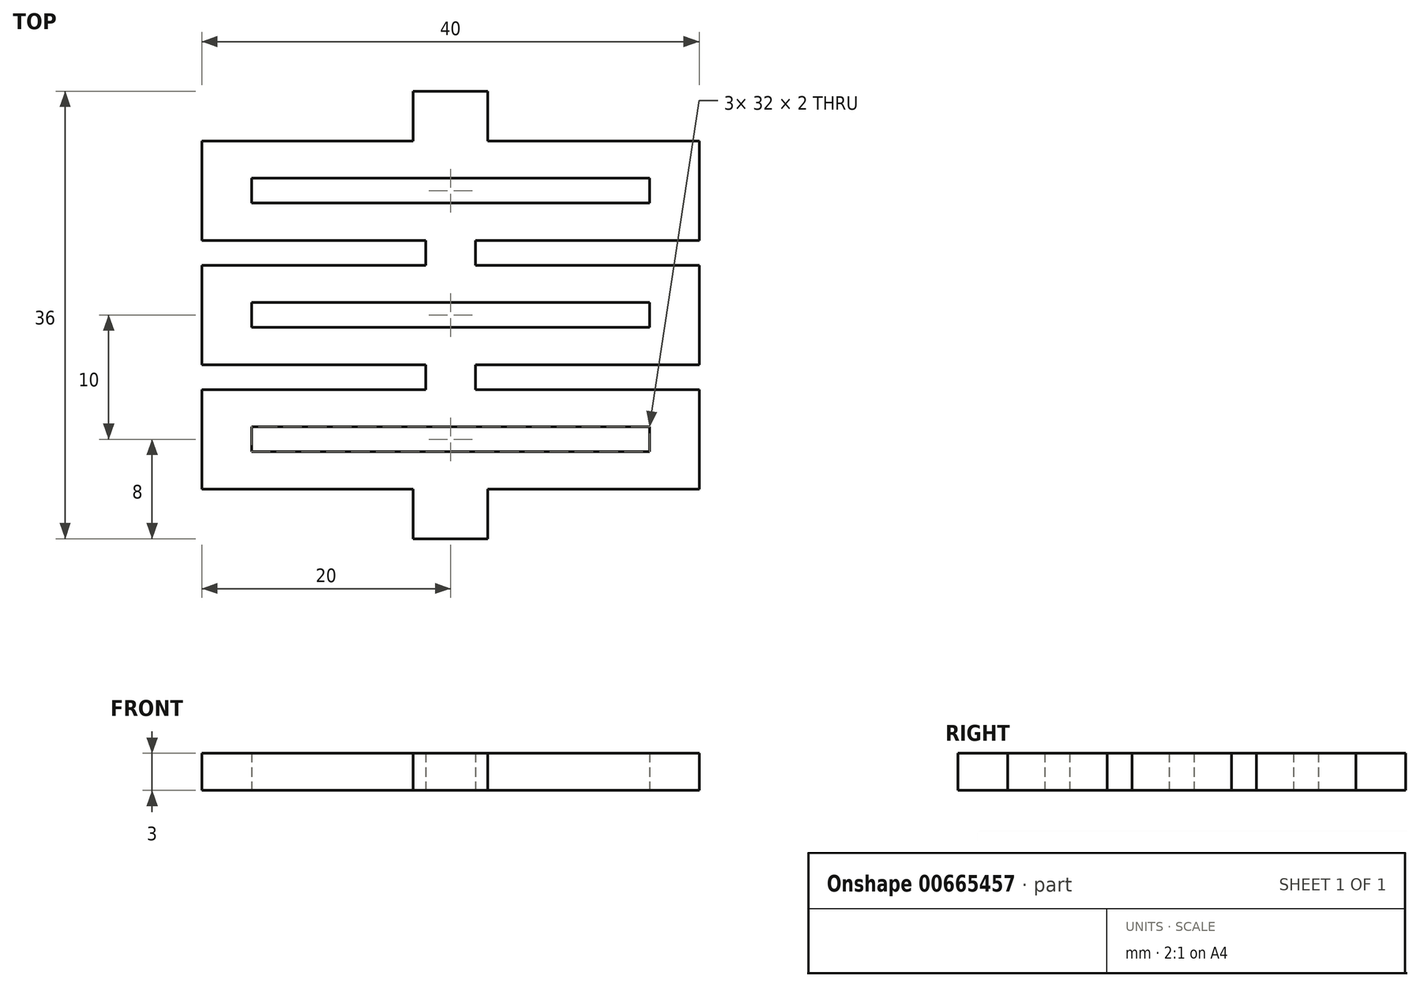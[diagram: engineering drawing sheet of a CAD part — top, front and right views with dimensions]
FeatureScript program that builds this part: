
annotation { "Feature Type Name" : "Feature", "Feature Type Description" : "" }
export const myFeature = defineFeature(function(context is Context, id is Id, definition is map)
    precondition{}
    {
        {
            var Q0;
            Q0=qCreatedBy(makeId("Top.planeOp"),FACE);
            var sketch = newSketch(context, id + "F0", { "sketchPlane" : qUnion([Q0])});
            skLineSegment(sketch, "E0.bottom", {"start": v(-3, 0) * mm, "end": v(0, 0) * mm});
            skLineSegment(sketch, "E0.top", {"start": v(-3, -4) * mm, "end": v(0, -4) * mm});
            skLineSegment(sketch, "E0.left", {"start": v(-3, 0) * mm, "end": v(-3, -4) * mm});
            skLineSegment(sketch, "E1.bottom", {"start": v(-20, -4) * mm, "end": v(0, -4) * mm});
            skLineSegment(sketch, "E1.top", {"start": v(-20, -7) * mm, "end": v(0, -7) * mm});
            skLineSegment(sketch, "E1.left", {"start": v(-20, -4) * mm, "end": v(-20, -7) * mm});
            skLineSegment(sketch, "E2.bottom", {"start": v(-20, -7) * mm, "end": v(-16, -7) * mm});
            skLineSegment(sketch, "E2.top", {"start": v(-20, -9) * mm, "end": v(-16, -9) * mm});
            skLineSegment(sketch, "E2.left", {"start": v(-20, -7) * mm, "end": v(-20, -9) * mm});
            skLineSegment(sketch, "E2.right", {"start": v(-16, -7) * mm, "end": v(-16, -9) * mm});
            skLineSegment(sketch, "E3.bottom", {"start": v(-16, -9) * mm, "end": v(0, -9) * mm});
            skLineSegment(sketch, "E3.top", {"start": v(-20, -12) * mm, "end": v(0, -12) * mm});
            skLineSegment(sketch, "E3.left", {"start": v(-20, -9) * mm, "end": v(-20, -12) * mm});
            skLineSegment(sketch, "E4.bottom", {"start": v(-2, -12) * mm, "end": v(0, -12) * mm});
            skLineSegment(sketch, "E4.top", {"start": v(-2, -14) * mm, "end": v(0, -14) * mm});
            skLineSegment(sketch, "E4.left", {"start": v(-2, -12) * mm, "end": v(-2, -14) * mm});
            skLineSegment(sketch, "E5.bottom", {"start": v(-20, -14) * mm, "end": v(0, -14) * mm});
            skLineSegment(sketch, "E5.top", {"start": v(-20, -17) * mm, "end": v(0, -17) * mm});
            skLineSegment(sketch, "E5.left", {"start": v(-20, -14) * mm, "end": v(-20, -17) * mm});
            skLineSegment(sketch, "E6.bottom", {"start": v(-20, -17) * mm, "end": v(-16, -17) * mm});
            skLineSegment(sketch, "E6.top", {"start": v(-20, -19) * mm, "end": v(-16, -19) * mm});
            skLineSegment(sketch, "E6.left", {"start": v(-20, -17) * mm, "end": v(-20, -19) * mm});
            skLineSegment(sketch, "E6.right", {"start": v(-16, -17) * mm, "end": v(-16, -19) * mm});
            skLineSegment(sketch, "E7.bottom", {"start": v(-20, -19) * mm, "end": v(0, -19) * mm});
            skLineSegment(sketch, "E7.top", {"start": v(-20, -22) * mm, "end": v(0, -22) * mm});
            skLineSegment(sketch, "E7.left", {"start": v(-20, -19) * mm, "end": v(-20, -22) * mm});
            skLineSegment(sketch, "E8.bottom", {"start": v(-2, -22) * mm, "end": v(0, -22) * mm});
            skLineSegment(sketch, "E8.top", {"start": v(-2, -24) * mm, "end": v(0, -24) * mm});
            skLineSegment(sketch, "E8.left", {"start": v(-2, -22) * mm, "end": v(-2, -24) * mm});
            skLineSegment(sketch, "E9.bottom", {"start": v(-20, -24) * mm, "end": v(0, -24) * mm});
            skLineSegment(sketch, "E9.top", {"start": v(-20, -27) * mm, "end": v(0, -27) * mm});
            skLineSegment(sketch, "E9.left", {"start": v(-20, -24) * mm, "end": v(-20, -27) * mm});
            skLineSegment(sketch, "E10.bottom", {"start": v(-20, -27) * mm, "end": v(-16, -27) * mm});
            skLineSegment(sketch, "E10.top", {"start": v(-20, -29) * mm, "end": v(-16, -29) * mm});
            skLineSegment(sketch, "E10.left", {"start": v(-20, -27) * mm, "end": v(-20, -29) * mm});
            skLineSegment(sketch, "E10.right", {"start": v(-16, -27) * mm, "end": v(-16, -29) * mm});
            skLineSegment(sketch, "E11.bottom", {"start": v(-20, -29) * mm, "end": v(0, -29) * mm});
            skLineSegment(sketch, "E11.top", {"start": v(-20, -32) * mm, "end": v(0, -32) * mm});
            skLineSegment(sketch, "E11.left", {"start": v(-20, -29) * mm, "end": v(-20, -32) * mm});
            skLineSegment(sketch, "E12.bottom", {"start": v(-3, -32) * mm, "end": v(0, -32) * mm});
            skLineSegment(sketch, "E12.top", {"start": v(-3, -36) * mm, "end": v(0, -36) * mm});
            skLineSegment(sketch, "E12.left", {"start": v(-3, -32) * mm, "end": v(-3, -36) * mm});
            skLineSegment(sketch, "E13", {"start": v(0, 0) * mm, "end": v(0, -60.03) * mm, "construction": true});
            skLineSegment(sketch, "E14.MirrorCS", {"start": v(20, -7) * mm, "end": v(20, -9) * mm});
            skLineSegment(sketch, "E15.MirrorCS", {"start": v(20, -17) * mm, "end": v(20, -19) * mm});
            skLineSegment(sketch, "E16.MirrorCS", {"start": v(20, -27) * mm, "end": v(20, -29) * mm});
            skLineSegment(sketch, "E17.MirrorCS", {"start": v(16, -27) * mm, "end": v(16, -29) * mm});
            skLineSegment(sketch, "E18.MirrorCS", {"start": v(2, -22) * mm, "end": v(0, -22) * mm});
            skLineSegment(sketch, "E19.MirrorCS", {"start": v(2, -24) * mm, "end": v(0, -24) * mm});
            skLineSegment(sketch, "E20.MirrorCS", {"start": v(16, -7) * mm, "end": v(16, -9) * mm});
            skLineSegment(sketch, "E21.MirrorCS", {"start": v(2, -14) * mm, "end": v(0, -14) * mm});
            skLineSegment(sketch, "E22.MirrorCS", {"start": v(2, -22) * mm, "end": v(2, -24) * mm});
            skLineSegment(sketch, "E23.MirrorCS", {"start": v(2, -12) * mm, "end": v(2, -14) * mm});
            skLineSegment(sketch, "E24.MirrorCS", {"start": v(2, -12) * mm, "end": v(0, -12) * mm});
            skLineSegment(sketch, "E25.MirrorCS", {"start": v(16, -17) * mm, "end": v(16, -19) * mm});
            skLineSegment(sketch, "E26.MirrorCS", {"start": v(3, -4) * mm, "end": v(0, -4) * mm});
            skLineSegment(sketch, "E27.MirrorCS", {"start": v(20, -17) * mm, "end": v(16, -17) * mm});
            skLineSegment(sketch, "E28.MirrorCS", {"start": v(20, -27) * mm, "end": v(16, -27) * mm});
            skLineSegment(sketch, "E29.MirrorCS", {"start": v(3, -32) * mm, "end": v(0, -32) * mm});
            skLineSegment(sketch, "E30.MirrorCS", {"start": v(20, -24) * mm, "end": v(20, -27) * mm});
            skLineSegment(sketch, "E31.MirrorCS", {"start": v(20, -22) * mm, "end": v(0, -22) * mm});
            skLineSegment(sketch, "E32.MirrorCS", {"start": v(20, -29) * mm, "end": v(16, -29) * mm});
            skLineSegment(sketch, "E33.MirrorCS", {"start": v(20, -7) * mm, "end": v(16, -7) * mm});
            skLineSegment(sketch, "E34.MirrorCS", {"start": v(3, -36) * mm, "end": v(0, -36) * mm});
            skLineSegment(sketch, "E35.MirrorCS", {"start": v(20, -7) * mm, "end": v(0, -7) * mm});
            skLineSegment(sketch, "E36.MirrorCS", {"start": v(20, -29) * mm, "end": v(0, -29) * mm});
            skLineSegment(sketch, "E37.MirrorCS", {"start": v(20, -14) * mm, "end": v(0, -14) * mm});
            skLineSegment(sketch, "E38.MirrorCS", {"start": v(20, -29) * mm, "end": v(20, -32) * mm});
            skLineSegment(sketch, "E39.MirrorCS", {"start": v(20, -24) * mm, "end": v(0, -24) * mm});
            skLineSegment(sketch, "E40.MirrorCS", {"start": v(20, -19) * mm, "end": v(16, -19) * mm});
            skLineSegment(sketch, "E41.MirrorCS", {"start": v(20, -17) * mm, "end": v(0, -17) * mm});
            skLineSegment(sketch, "E42.MirrorCS", {"start": v(16, -9) * mm, "end": v(0, -9) * mm});
            skLineSegment(sketch, "E43.MirrorCS", {"start": v(20, -19) * mm, "end": v(0, -19) * mm});
            skLineSegment(sketch, "E44.MirrorCS", {"start": v(20, -12) * mm, "end": v(0, -12) * mm});
            skLineSegment(sketch, "E45.MirrorCS", {"start": v(20, -9) * mm, "end": v(16, -9) * mm});
            skLineSegment(sketch, "E46.MirrorCS", {"start": v(3, 0) * mm, "end": v(3, -4) * mm});
            skLineSegment(sketch, "E47.MirrorCS", {"start": v(20, -19) * mm, "end": v(20, -22) * mm});
            skLineSegment(sketch, "E48.MirrorCS", {"start": v(3, -32) * mm, "end": v(3, -36) * mm});
            skLineSegment(sketch, "E49.MirrorCS", {"start": v(20, -4) * mm, "end": v(20, -7) * mm});
            skLineSegment(sketch, "E50.MirrorCS", {"start": v(20, -14) * mm, "end": v(20, -17) * mm});
            skLineSegment(sketch, "E51.MirrorCS", {"start": v(20, -9) * mm, "end": v(20, -12) * mm});
            skLineSegment(sketch, "E52.MirrorCS", {"start": v(20, -4) * mm, "end": v(0, -4) * mm});
            skLineSegment(sketch, "E53.MirrorCS", {"start": v(20, -32) * mm, "end": v(0, -32) * mm});
            skLineSegment(sketch, "E54.MirrorCS", {"start": v(20, -27) * mm, "end": v(0, -27) * mm});
            skLineSegment(sketch, "E55.MirrorCS", {"start": v(3, 0) * mm, "end": v(0, 0) * mm});
            skSolve(sketch);
        }
        {
            var Q0;
            Q0 = qSketchRegion(id + "F0", true);
            extrude(context, id + "F1", {"entities" : qUnion([Q0]), "depth" : 3 * mm, "offsetDistance" : 25 * mm});
        }
    });
